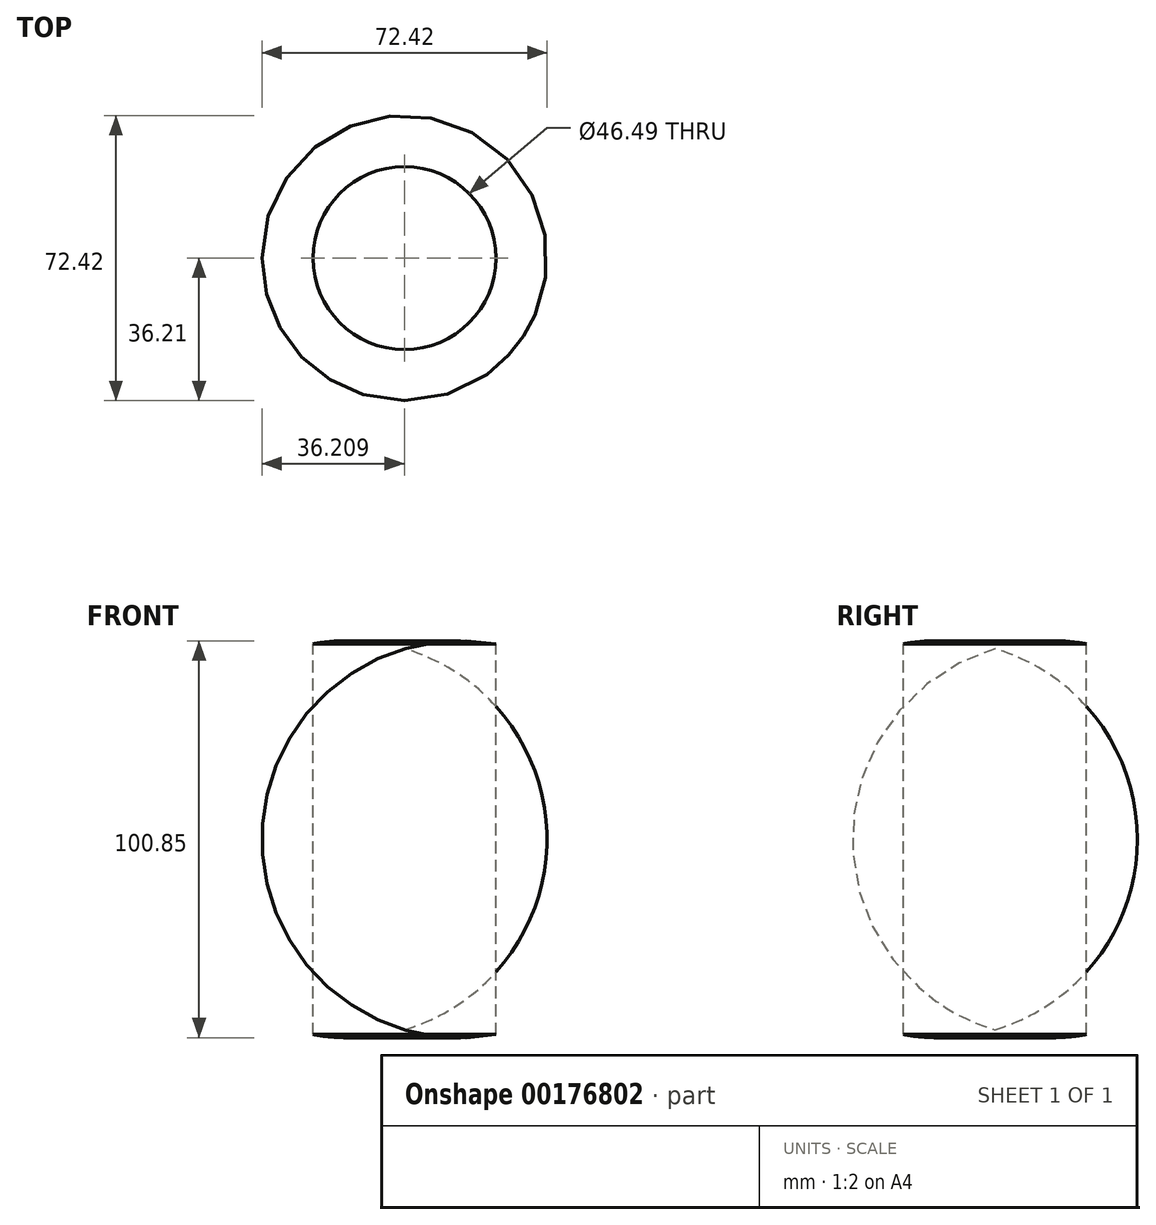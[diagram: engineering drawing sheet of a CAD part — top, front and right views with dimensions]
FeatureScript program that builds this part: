
annotation { "Feature Type Name" : "Feature", "Feature Type Description" : "" }
export const myFeature = defineFeature(function(context is Context, id is Id, definition is map)
    precondition{}
    {
        {
            var Q0;
            Q0=qCreatedBy(makeId("Front.planeOp"),FACE);
            var sketch = newSketch(context, id + "F0", { "sketchPlane" : qUnion([Q0])});
            skLineSegment(sketch, "E0", {"start": v(-47.23, 56.47) * mm, "end": v(-47.23, -42.76) * mm});
            skLineSegment(sketch, "E1", {"start": v(-23.99, 56.47) * mm, "end": v(-23.99, -42.76) * mm});
            skArc(sketch, "E2", {"start": v(-23.99, -42.76) * mm, "mid": v(17.42, 6.85) * mm, "end": v(-23.99, 56.47) * mm});
            skSolve(sketch);
        }
        {
            var Q0;
            Q0=makeQuery(id+"F0.imprint","IMPRINT",FACE,{"disambiguationData":[TD([[makeQuery(id+"F0.imprint","IMPRINT",EDGE,{"derivedFrom":sQuery(id+"F0.wireOp",EDGE,"E1")}),1.0]])]});
            var Q1;
            Q1=sQuery(id+"F0.wireOp",EDGE,"E0");
            revolve(context, id + "F1", {"entities" : qUnion([Q0]), "axis" : qUnion([Q1]), "revolveType" : RevolveType.FULL});
        }
    });
